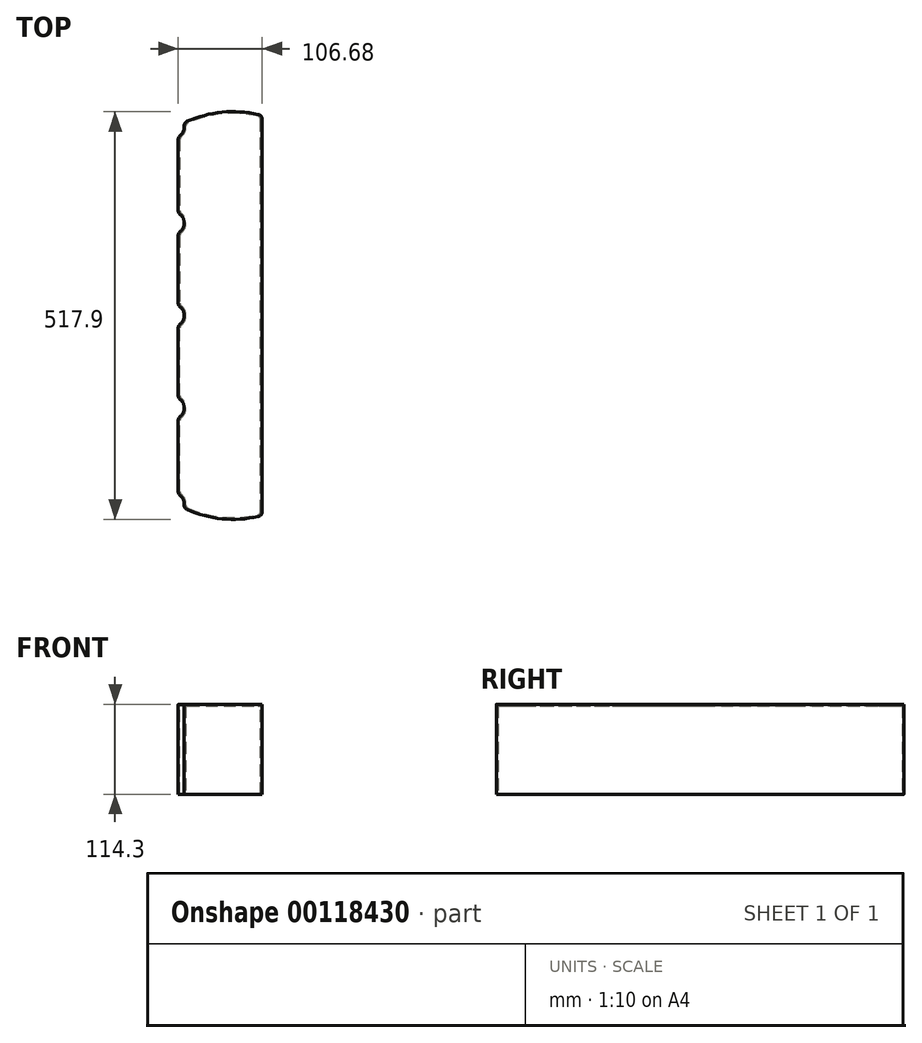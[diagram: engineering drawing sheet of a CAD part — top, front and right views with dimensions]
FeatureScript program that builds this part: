
annotation { "Feature Type Name" : "Feature", "Feature Type Description" : "" }
export const myFeature = defineFeature(function(context is Context, id is Id, definition is map)
    precondition{}
    {
        {
            var Q0;
            Q0=qCreatedBy(makeId("Top.planeOp"),FACE);
            var sketch = newSketch(context, id + "F0", { "sketchPlane" : qUnion([Q0])});
            skArc(sketch, "E0.1", {"start": v(-52.75, -230.66) * mm, "mid": v(-8.28, -242.26) * mm, "end": v(37.59, -239.46) * mm});
            skLineSegment(sketch, "E0.2", {"start": v(42.56, -233.26) * mm, "end": v(42.56, 16) * mm});
            skArc(sketch, "E1", {"start": v(-61.74, 5.1) * mm, "mid": v(-57.87, 9.97) * mm, "end": v(-56.5, 16.04) * mm});
            skArc(sketch, "E2", {"start": v(-61.74, -112.38) * mm, "mid": v(-56.5, -101.47) * mm, "end": v(-61.74, -90.57) * mm});
            skArc(sketch, "E3", {"start": v(-56.54, -224.39) * mm, "mid": v(-57.67, -217.8) * mm, "end": v(-61.74, -212.49) * mm});
            skLineSegment(sketch, "E4.trimOffspring", {"start": v(-64.12, -207.53) * mm, "end": v(-64.12, -117.33) * mm});
            skLineSegment(sketch, "E5.trimOffspring", {"start": v(-64.12, -85.6) * mm, "end": v(-64.12, 0.14) * mm});
            skPoint(sketch, "E6.visualSharp", {"position": v(-64.12, -210.95) * mm});
            skArc(sketch, "E6.filletArc", {"start": v(-64.12, -207.53) * mm, "mid": v(-63.5, -210.28) * mm, "end": v(-61.74, -212.49) * mm});
            skArc(sketch, "E7.filletArc", {"start": v(-56.54, -224.39) * mm, "mid": v(-55.64, -228.12) * mm, "end": v(-52.75, -230.66) * mm});
            skPoint(sketch, "E8.visualSharp", {"position": v(42.56, -238.27) * mm});
            skArc(sketch, "E8.filletArc", {"start": v(37.59, -239.46) * mm, "mid": v(41.16, -237.24) * mm, "end": v(42.56, -233.26) * mm});
            skPoint(sketch, "E9.visualSharp", {"position": v(-64.12, -113.91) * mm});
            skArc(sketch, "E9.filletArc", {"start": v(-61.74, -112.38) * mm, "mid": v(-63.5, -114.58) * mm, "end": v(-64.12, -117.33) * mm});
            skPoint(sketch, "E10.visualSharp", {"position": v(-64.12, -89.03) * mm});
            skArc(sketch, "E10.filletArc", {"start": v(-64.12, -85.6) * mm, "mid": v(-63.5, -88.36) * mm, "end": v(-61.74, -90.57) * mm});
            skPoint(sketch, "E11.visualSharp", {"position": v(-64.12, 3.56) * mm});
            skArc(sketch, "E11.filletArc", {"start": v(-61.74, 5.1) * mm, "mid": v(-63.5, 2.9) * mm, "end": v(-64.12, 0.14) * mm});
            skLineSegment(sketch, "E12", {"start": v(-64.7, 47.22) * mm, "end": v(-64.7, 47.22) * mm});
            skArc(sketch, "E13.MirrorCS", {"start": v(-56.54, 256.4) * mm, "mid": v(-55.64, 260.13) * mm, "end": v(-52.75, 262.66) * mm});
            skArc(sketch, "E14.MirrorCS", {"start": v(-61.74, 144.38) * mm, "mid": v(-63.5, 146.59) * mm, "end": v(-64.12, 149.34) * mm});
            skArc(sketch, "E15.MirrorCS", {"start": v(-64.12, 117.61) * mm, "mid": v(-63.5, 120.36) * mm, "end": v(-61.74, 122.57) * mm});
            skArc(sketch, "E16.MirrorCS", {"start": v(37.59, 271.47) * mm, "mid": v(41.16, 269.24) * mm, "end": v(42.56, 265.27) * mm});
            skArc(sketch, "E17.MirrorCS", {"start": v(-64.12, 239.53) * mm, "mid": v(-63.5, 242.28) * mm, "end": v(-61.74, 244.5) * mm});
            skArc(sketch, "E18.MirrorCS", {"start": v(-61.74, 26.9) * mm, "mid": v(-63.5, 29.11) * mm, "end": v(-64.12, 31.86) * mm});
            skArc(sketch, "E19.MirrorCS", {"start": v(-61.74, 26.9) * mm, "mid": v(-57.87, 22.03) * mm, "end": v(-56.5, 15.96) * mm});
            skArc(sketch, "E20.MirrorCS", {"start": v(-56.54, 256.4) * mm, "mid": v(-57.67, 249.8) * mm, "end": v(-61.74, 244.5) * mm});
            skPoint(sketch, "E21.MirrorP", {"position": v(-64.12, 242.95) * mm});
            skArc(sketch, "E22.MirrorCS", {"start": v(-61.74, 144.38) * mm, "mid": v(-56.5, 133.48) * mm, "end": v(-61.74, 122.57) * mm});
            skLineSegment(sketch, "E23.MirrorCS", {"start": v(-64.12, 239.53) * mm, "end": v(-64.12, 149.34) * mm});
            skPoint(sketch, "E24.MirrorP", {"position": v(42.56, 270.27) * mm});
            skPoint(sketch, "E25.MirrorP", {"position": v(-57.46, 260.5) * mm});
            skLineSegment(sketch, "E26.MirrorCS", {"start": v(42.56, 265.27) * mm, "end": v(42.56, 16) * mm});
            skLineSegment(sketch, "E27.MirrorCS", {"start": v(-64.12, 117.61) * mm, "end": v(-64.12, 31.86) * mm});
            skPoint(sketch, "E28.MirrorP", {"position": v(-64.12, 28.44) * mm});
            skArc(sketch, "E29.MirrorCS", {"start": v(-52.75, 262.66) * mm, "mid": v(-8.28, 274.26) * mm, "end": v(37.59, 271.47) * mm});
            skPoint(sketch, "E30.MirrorP", {"position": v(-64.12, 145.92) * mm});
            skSolve(sketch);
        }
        {
            var Q0;
            Q0=makeQuery(id+"F0.imprint","IMPRINT",FACE,{"disambiguationData":[TD([[makeQuery(id+"F0.imprint","IMPRINT",EDGE,{"derivedFrom":sQuery(id+"F0.wireOp",EDGE,"E0.1")}),1.0]])]});
            extrude(context, id + "F1", {"entities" : qUnion([Q0]), "depth" : 114.3 * mm});
        }
        {
            var Q0;
            Q0=makeQuery(id+"F1.opExtrude","CAP_FACE",FACE,{"disambiguationData":[OSD([sQuery(id+"F0.wireOp",EDGE,"E0.1"),sQuery(id+"F0.wireOp",EDGE,"E0.2"),sQuery(id+"F0.wireOp",EDGE,"E1"),sQuery(id+"F0.wireOp",EDGE,"E2"),sQuery(id+"F0.wireOp",EDGE,"E3"),sQuery(id+"F0.wireOp",EDGE,"E4.trimOffspring"),sQuery(id+"F0.wireOp",EDGE,"E5.trimOffspring"),sQuery(id+"F0.wireOp",EDGE,"E6.filletArc"),sQuery(id+"F0.wireOp",EDGE,"E7.filletArc"),sQuery(id+"F0.wireOp",EDGE,"E8.filletArc"),sQuery(id+"F0.wireOp",EDGE,"E9.filletArc"),sQuery(id+"F0.wireOp",EDGE,"E10.filletArc"),sQuery(id+"F0.wireOp",EDGE,"E11.filletArc"),sQuery(id+"F0.wireOp",EDGE,"E13.MirrorCS"),sQuery(id+"F0.wireOp",EDGE,"E14.MirrorCS"),sQuery(id+"F0.wireOp",EDGE,"E15.MirrorCS"),sQuery(id+"F0.wireOp",EDGE,"E16.MirrorCS"),sQuery(id+"F0.wireOp",EDGE,"E17.MirrorCS"),sQuery(id+"F0.wireOp",EDGE,"E18.MirrorCS"),sQuery(id+"F0.wireOp",EDGE,"E19.MirrorCS"),sQuery(id+"F0.wireOp",EDGE,"E20.MirrorCS"),sQuery(id+"F0.wireOp",EDGE,"E22.MirrorCS"),sQuery(id+"F0.wireOp",EDGE,"E23.MirrorCS"),sQuery(id+"F0.wireOp",EDGE,"E26.MirrorCS"),sQuery(id+"F0.wireOp",EDGE,"E27.MirrorCS"),sQuery(id+"F0.wireOp",EDGE,"E29.MirrorCS")])],"isStart":true});
            shell(context, id + "F2", {"entities" : qUnion([Q0]), "thickness" : 2.03 * mm});
        }
    });
